# Revit family: Perry Corner Box Window
name_source: partatom
category: Windows
revit_build: Autodesk Revit 2014 (Build: 20130308_1515(x64)
units: mm (PartAtom-declared; Revit-internal decimal feet)

## types (28) — shared parameters
Analytic Construction = <None>
Assembly Code = B2020100
Frame Depth = 0' - 1 1/2"
Glass Pane Material = Glass
Operable Frame Width = 0' - 3"
Rough Height = 5' - 3"
Sash Material = Sash
Wall Closure = By host
Window Inset = 0' - 0 3/4"

## per-type parameters (varying)
| type | Casement window material | Default Sill Height | Depth | Description | Height | Rough Width | Width |
| 36" x 48" | Aluminum, Anodized Bronze | 2' - 0" | 0' - 9 1/2" | SBF | 6' - 0" | 11' - 11 7/16" | 1' - 3" |
| 24" x 48" | <By Category> | 3' - 0" | 0' - 11 1/4" |  | 4' - 0" | 11' - 2 1/4" | 2' - 0" |
| 24" x 24" | <By Category> | 3' - 0" | 0' - 11 1/4" |  | 2' - 0" | 11' - 2 1/4" | 2' - 0" |
| 16" x 24" | <By Category> | 3' - 0" | 0' - 11 1/4" |  | 2' - 0" | 11' - 2 1/4" | 1' - 4" |
| 16" x 48" | <By Category> | 3' - 0" | 0' - 11 1/4" |  | 4' - 0" | 11' - 2 1/4" | 1' - 4" |
| 16" x 72" | <By Category> | 1' - 0" | 0' - 11 1/4" |  | 6' - 0" | 11' - 2 1/4" | 1' - 4" |
| 24" x 72" | <By Category> | 1' - 0" | 0' - 11 1/4" |  | 6' - 0" | 11' - 2 1/4" | 2' - 0" |
| 36" x 24" | <By Category> | 3' - 0" | 0' - 11 1/4" |  | 2' - 0" | 11' - 2 1/4" | 3' - 0" |
| 36" x 72" | <By Category> | 1' - 0" | 0' - 11 1/4" |  | 6' - 0" | 11' - 2 1/4" | 3' - 0" |
| 3' 5" x5' 3" | <By Category> | 3' - 6" | 0' - 11 1/4" |  | 5' - 3" | 11' - 2 1/4" | 9' - 3" |
| 4' 6" x 5'3" | <By Category> | 3' - 0" | 0' - 11 1/4" |  | 5' - 3" | 11' - 2 1/4" | 4' - 6" |
| 5' 3" x 6' 2 | <By Category> | 2' - 0" | 0' - 11 1/4" |  | 5' - 3" | 11' - 2 1/4" | 6' - 0" |
| 3' 7" | <By Category> | 2' - 0" | 0' - 11 1/4" |  | 6' - 0" | 11' - 2 1/4" | 3' - 7" |
| 3' 8" short | <By Category> | 2' - 0" | 0' - 11 1/4" |  | 3' - 9 3/8" | 11' - 2 1/4" | 3' - 8" |
| 3' 8" | <By Category> | 2' - 0" | 0' - 11 1/4" |  | 6' - 0" | 11' - 2 1/4" | 3' - 8" |
| 4' 6" | <By Category> | 3' - 6" | 0' - 11 1/4" |  | 8' - 3" | 11' - 2 1/4" | 4' - 6" |
| 2'9" | <By Category> | 3' - 6" | 0' - 11 1/4" |  | 4' - 0" | 11' - 2 1/4" | 2' - 9" |
| 3' 6.5 | <By Category> | 3' - 6" | 0' - 11 1/4" |  | 8' - 3" | 11' - 2 1/4" | 4' - 0" |
| 6' | <By Category> | 2' - 6" | 0' - 11 1/4" |  | 5' - 0" | 11' - 2 1/4" | 6' - 0" |
| 3' 10" 2 | <By Category> | 2' - 6" | 0' - 11 1/4" |  | 5' - 0" | 11' - 2 1/4" | 6' - 0" |
| 1' 3/4" | <By Category> | 3' - 6" | 0' - 11 1/4" |  | 4' - 0" | 11' - 2 1/4" | 1' - 0 3/4" |
| 9 | <By Category> | 2' - 0" | 0' - 11 1/4" |  | 6' - 0" | 11' - 2 1/4" | 9' - 6" |
| 3' 10" | <By Category> | 2' - 0" | 0' - 11 1/4" |  | 6' - 0" | 11' - 2 1/4" | 3' - 10" |
| 3' 1" | <By Category> | 2' - 0" | 0' - 11 1/4" |  | 6' - 0" | 11' - 2 1/4" | 3' - 1" |
| 1' 3" | <By Category> | 3' - 6" | 0' - 11 1/4" |  | 3' - 0" | 11' - 2 1/4" | 1' - 0 3/4" |
| 3' 5" | <By Category> | 3' - 6" | 0' - 11 1/4" |  | 4' - 11" | 11' - 2 1/4" | 9' - 3" |
| 2' 10 1/2" x 6' | <By Category> | 2' - 0" | 0' - 11 1/4" |  | 6' - 0" | 11' - 2 1/4" | 3' - 0" |
| 4' 6" x 6' | <By Category> | 2' - 0" | 0' - 11 1/4" |  | 6' - 0" | 11' - 2 1/4" | 6' - 0" |

## geometry (parser evidence)
native form markers: Sweep x1
no freeform markers — native parametric forms only
